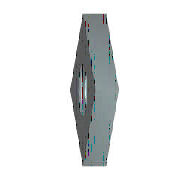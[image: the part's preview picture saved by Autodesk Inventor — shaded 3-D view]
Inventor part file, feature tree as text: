
AUTODESK INVENTOR PART (.ipt)
format: ipt  version: 2017 (Build 210142000, 142)  size: 124,416 bytes
history: native  units: mm (DEFAULTED — no unit token found)
features: sketch x2, hole x1, other x1, plane x1
ambient origin geometry x8: Origin, YZ Plane, XZ Plane, XY Plane, X Axis, Y Axis, Z Axis, Center Point
bodies: Solid1 (feature_tree), Body (feature_tree)
feature tree (5):
  hole  "Thread"  [1 undecoded]
  other  "Work Axis1"
  plane  "Work Plane1"
  sketch  "Sketch1"  dims[d0=7.778175mm d1=1.78mm d2=0.0mm]
  sketch  "Sketch2"  dims[d20=2.459mm d21=6.0mm d22=4.0mm d23=2.0mm d24=14.3117mm d25=8.0mm d26=20.594885mm d3=0.270633mm d4=30.0deg d5=0.270633mm d6=30.0deg d8=0.0mm d9=0.0mm d34=0.0mm d35=0.270633mm d36=0.270633mm d37=90.0deg d38=0.0mm]
note: 1 required parameter value undecoded (feature->parameter linkage not recoverable at this tier; creation-order binding heuristic only, values carry confidence <= 0.55)
